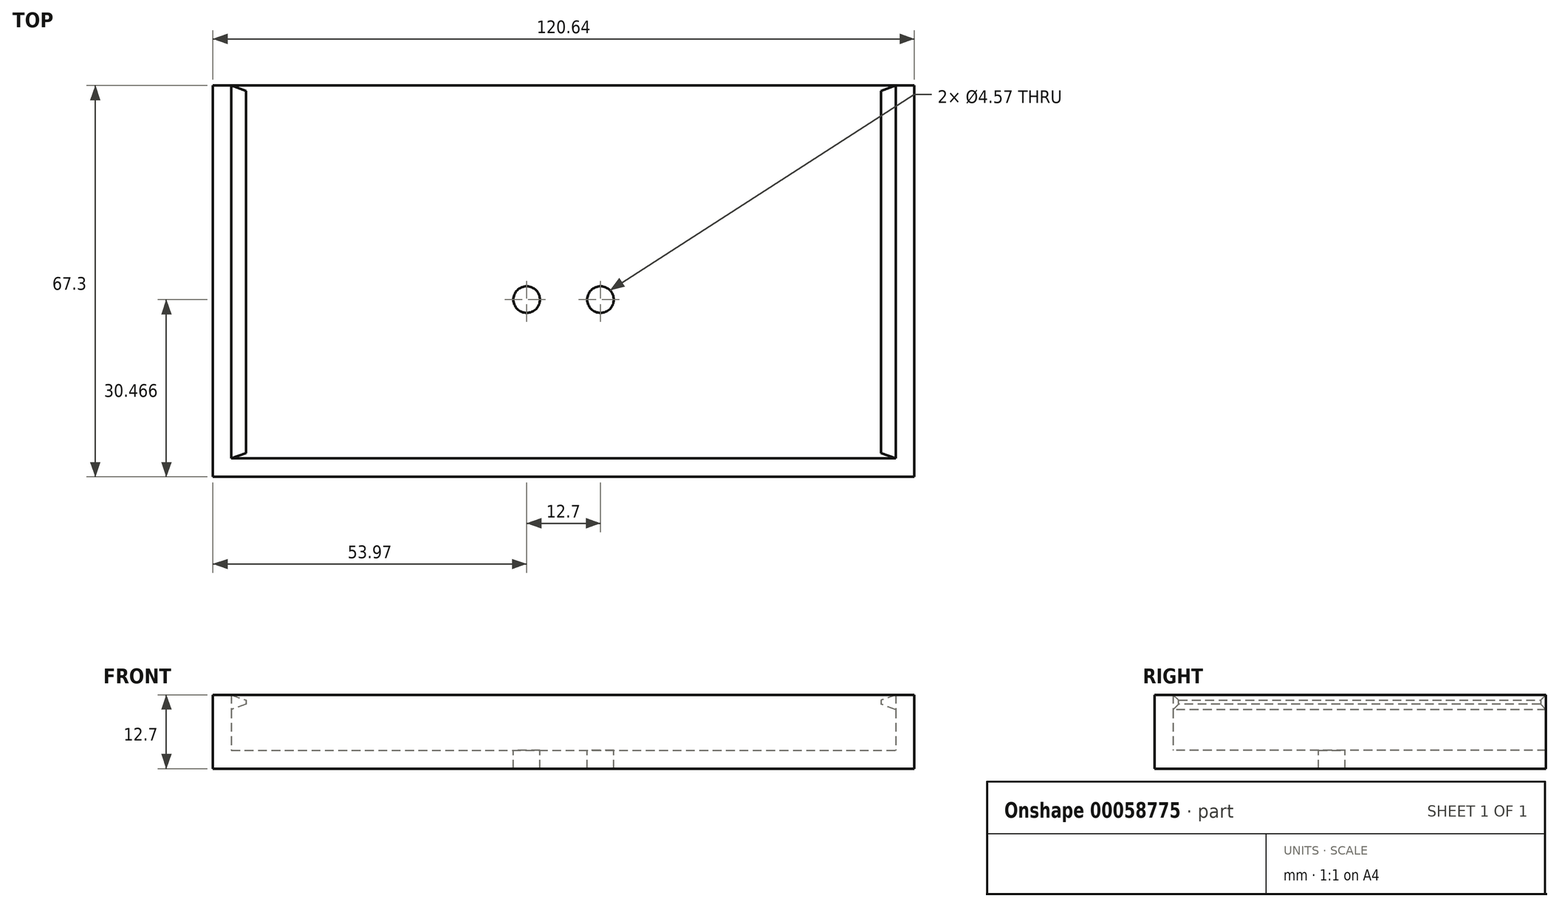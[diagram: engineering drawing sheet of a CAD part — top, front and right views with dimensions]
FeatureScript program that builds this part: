
annotation { "Feature Type Name" : "Feature", "Feature Type Description" : "" }
export const myFeature = defineFeature(function(context is Context, id is Id, definition is map)
    precondition{}
    {
        {
            var Q0;
            Q0=qCreatedBy(makeId("Top.planeOp"),FACE);
            var sketch = newSketch(context, id + "F0", { "sketchPlane" : qUnion([Q0])});
            skLineSegment(sketch, "E0.rect.bottom", {"start": v(-60.32, 33.66) * mm, "end": v(60.33, 33.66) * mm});
            skLineSegment(sketch, "E0.rect.top", {"start": v(-60.33, -33.66) * mm, "end": v(60.32, -33.66) * mm});
            skLineSegment(sketch, "E0.rect.left", {"start": v(-60.32, 33.66) * mm, "end": v(-60.33, -33.66) * mm});
            skLineSegment(sketch, "E0.rect.right", {"start": v(60.33, 33.66) * mm, "end": v(60.32, -33.66) * mm});
            skPoint(sketch, "E0.rect.middle", {"position": v(0, 0) * mm});
            skSolve(sketch);
        }
        {
            var Q0;
            Q0=makeQuery(id+"F0.imprint","IMPRINT",FACE,{"disambiguationData":[TD([[makeQuery(id+"F0.imprint","IMPRINT",EDGE,{"derivedFrom":sQuery(id+"F0.wireOp",EDGE,"E0.rect.bottom")}),-1.0]])]});
            extrude(context, id + "F1", {"entities" : qUnion([Q0]), "depth" : 12.7 * mm, "hasSecondDirection" : true, "secondDirectionOppositeDirection" : true, "secondDirectionDepth" : 6.35 * mm, "offsetDistance" : 25.4 * mm, "symmetric" : true});
        }
        {
            var Q0;
            Q0=makeQuery(id+"F1.opExtrude","CAP_FACE",FACE,{"disambiguationData":[OSD([sQuery(id+"F0.wireOp",EDGE,"E0.rect.bottom"),sQuery(id+"F0.wireOp",EDGE,"E0.rect.top"),sQuery(id+"F0.wireOp",EDGE,"E0.rect.left"),sQuery(id+"F0.wireOp",EDGE,"E0.rect.right")])],"isStart":false});
            var Q1;
            Q1=makeQuery(id+"F1.opExtrude","SWEPT_FACE",FACE,{"disambiguationData":[OSD([sQuery(id+"F0.wireOp",EDGE,"E0.rect.bottom")])]});
            shell(context, id + "F2", {"entities" : qUnion([Q0, Q1]), "thickness" : 3.17 * mm});
        }
        {
            var Q0;
            Q0=makeQuery(id+"F2.opShell","OFFSET_FACE",FACE,{"disambiguationData":[OSD([sQuery(id+"F0.wireOp",EDGE,"E0.rect.left")])]});
            var sketch = newSketch(context, id + "F3", { "sketchPlane" : qUnion([Q0])});
            skPoint(sketch, "E1", {"position": v(33.65, 6.35) * mm});
            skLineSegment(sketch, "E2", {"start": v(33.65, 6.35) * mm, "end": v(33.65, 3.81) * mm});
            skLineSegment(sketch, "E3", {"start": v(33.65, 3.8) * mm, "end": v(-30.48, 3.8) * mm});
            skPoint(sketch, "E3.endSnap0", {"position": v(-30.48, 1.59) * mm});
            skSolve(sketch);
        }
        {
            var Q0;
            Q0=makeQuery(id+"F3.imprint","IMPRINT",FACE,{"disambiguationData":[TD([[makeQuery(id+"F3.imprint","IMPRINT",EDGE,{"derivedFrom":sQuery(id+"F3.wireOp",EDGE,"E2")}),-1.0]])]});
            extrude(context, id + "F4", {"entities" : qUnion([Q0]), "depth" : 2.54 * mm, "hasDraft" : true, "draftAngle" : 20 * degree, "draftPullDirection" : true});
        }
        {
            var Q0;
            Q0=makeQuery(id+"F4.opExtrude","SWEPT_BODY",BODY,{"disambiguationData":[OSD([sQuery(id+"F0.wireOp",EDGE,"E0.rect.top"),sQuery(id+"F0.wireOp",EDGE,"E0.rect.left"),sQuery(id+"F3.wireOp",EDGE,"E2"),sQuery(id+"F3.wireOp",EDGE,"E3")])]});
            var Q1;
            Q1=qCreatedBy(makeId("Right.planeOp"),FACE);
            mirror(context, id + "F5", {"operationType" : NewBodyOperationType.ADD, "entities" : qUnion([Q0]), "mirrorPlane" : qUnion([Q1])});
        }
        {
            var Q0;
            Q0=makeQuery(id+"F2.opShell","OFFSET_FACE",FACE,{"disambiguationData":[OSD([sQuery(id+"F0.wireOp",EDGE,"E0.rect.bottom"),sQuery(id+"F0.wireOp",EDGE,"E0.rect.top"),sQuery(id+"F0.wireOp",EDGE,"E0.rect.left"),sQuery(id+"F0.wireOp",EDGE,"E0.rect.right")])]});
            var sketch = newSketch(context, id + "F6", { "sketchPlane" : qUnion([Q0])});
            skPoint(sketch, "E4", {"position": v(0, -3.18) * mm});
            skPoint(sketch, "E5", {"position": v(-6.35, -3.18) * mm});
            skPoint(sketch, "E6", {"position": v(6.35, -3.18) * mm});
            skCircle(sketch, "E7", {"center": v(-6.35, -3.18) * mm, "radius": 2.29 * mm});
            skCircle(sketch, "E8", {"center": v(6.35, -3.18) * mm, "radius": 2.29 * mm});
            skSolve(sketch);
        }
        {
            var Q0;
            Q0=makeQuery(id+"F6.imprint","IMPRINT",FACE,{"disambiguationData":[TD([[makeQuery(id+"F6.imprint","IMPRINT",EDGE,{"derivedFrom":sQuery(id+"F6.wireOp",EDGE,"E7")}),1.0]])]});
            var Q1;
            Q1=makeQuery(id+"F6.imprint","IMPRINT",FACE,{"disambiguationData":[TD([[makeQuery(id+"F6.imprint","IMPRINT",EDGE,{"derivedFrom":sQuery(id+"F6.wireOp",EDGE,"E8")}),1.0]])]});
            extrude(context, id + "F7", {"entities" : qUnion([Q0, Q1]), "operationType" : NewBodyOperationType.REMOVE, "oppositeDirection" : true, "depth" : 25.4 * mm});
        }
    });
